# Revit family: PRD_FrankeWS_WCSqttngPns_CAMPUSMountingSupportForSquatToilet_ZCMPX0011
name_source: partatom
category: Plumbing Fixtures
revit_build: Autodesk Revit 2018 (Build: 20190510_1515(x64)
units: mm (PartAtom-declared; Revit-internal decimal feet)

## family parameters
Cut with Voids When Loaded = Yes
Host = Face
OmniClass Number = 23.45.05.21.11.21
OmniClass Title = Urinals
Part Type = Normal
Room Calculation Point = No
Round Connector Dimension = Use Diameter
Shared = Yes

## types (1)
- ZCMPX0011
    AssetType = Fixed
    BIMObjectName = PRD_AR_WCSquattingPans_CAMPUSmountingSupportForSquatToilet_ZCMPX0011
    Category = Pr_40_20_93_96, WC squatting pans
    Default Elevation = 1100 mm
    Description = Mounting support for squat pan, made from styrofoam. Fitting foam glue by client.
    DurationUnit = year
    Features = styrofoam
    GeneralMaterial = PRD_AR_Styrofoam
    GrossWeight = 2.50 kg
    IfcExportAs = IfcSanitaryTerminalType
    IfcExportType = USERDEFINED
    Manufacturer = KWC Group AG
    ManufacturerName = KWC Group AG
    ManufacturerURL = www.kwc.com
    Material = Styrofoam
    Model = ZCMPX0011
    ModelNumber = 2030027861
    ModelReference = ZCMPX0011
    Name = CAMPUS Mounting support for squat toilet ZCMPX0011
    NetWeight = 2.20 kg
    NominalDepth = 680 mm  [stored 2.23097 ft]
    NominalHeight = 200 mm  [stored 0.656168 ft]
    NominalLength = 0 mm  [stored 0 ft]
    NominalWidth = 680 mm  [stored 2.23097 ft]
    ProductCode = 205.0638.904
    ProductInformation = https://pim.kwc.com
    Quantity = 1
    QuantityUom = Piece
    Size = 680 x 200 x 680 mm (W x H x D)
    Status = New
    TailorMade = No
    URL = www.kwc.com
    Uniclass2015Code = Pr_40_20_93_96
    Uniclass2015Title = WC squatting pans
    Uniclass2015Version = Products v1.23
    Version = 1
    WarrantyDurationUnit = year

note: [stored X ft] marks values corroborated as IEEE doubles in the binary element streams (Revit-internal decimal feet)

## geometry (parser evidence)
native form markers: Sweep x5
no freeform markers — native parametric forms only
